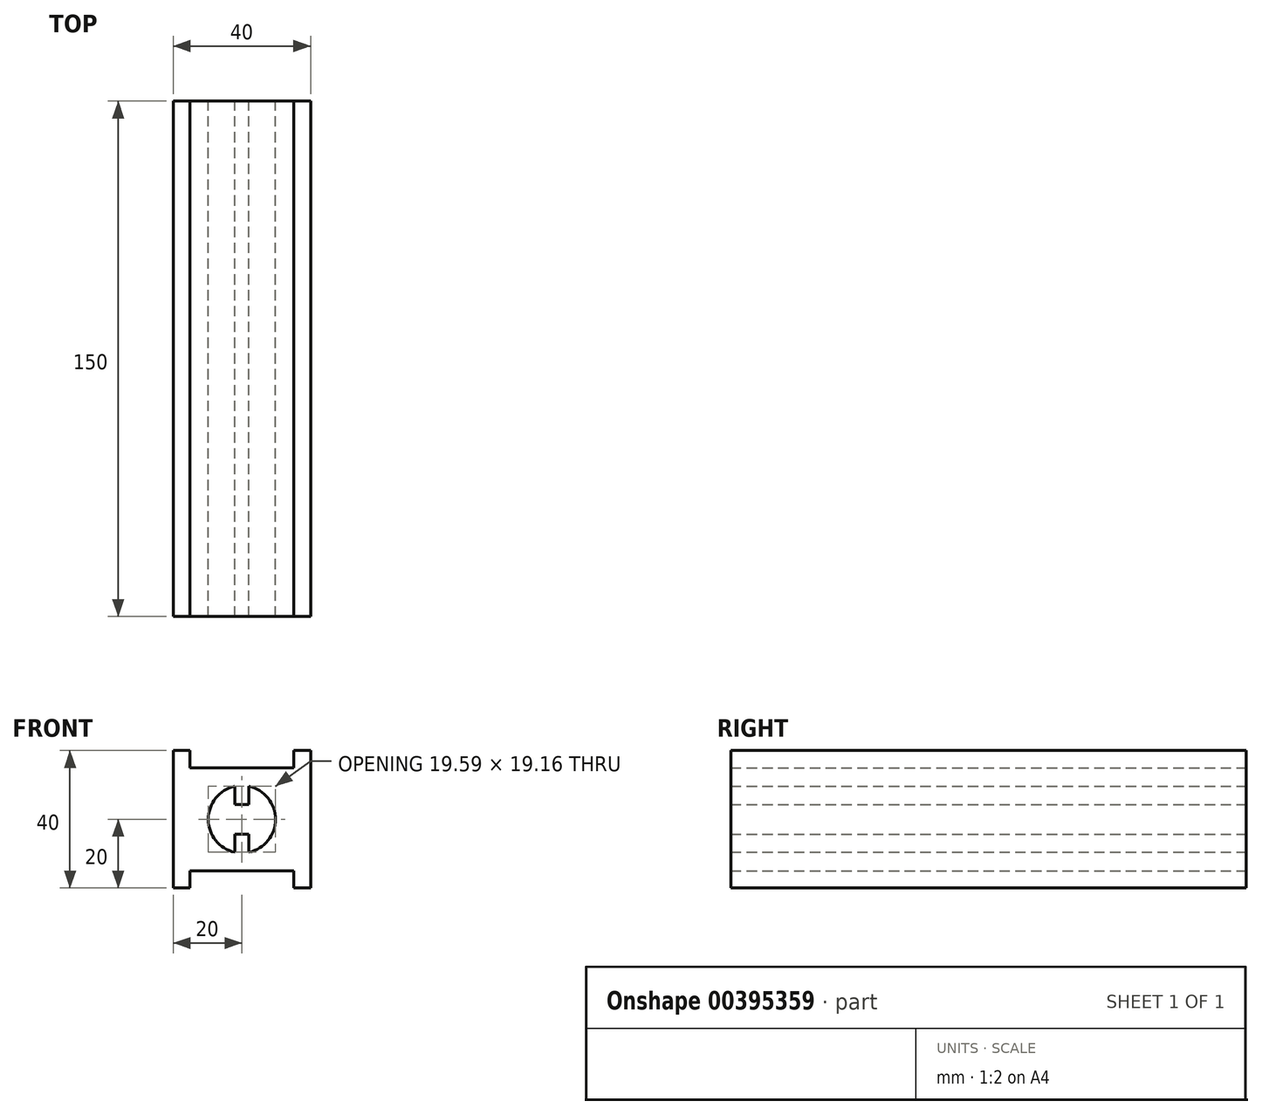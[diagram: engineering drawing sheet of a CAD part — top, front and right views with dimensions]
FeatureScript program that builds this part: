
annotation { "Feature Type Name" : "Feature", "Feature Type Description" : "" }
export const myFeature = defineFeature(function(context is Context, id is Id, definition is map)
    precondition{}
    {
        {
            var Q0;
            Q0=qCreatedBy(makeId("Front.planeOp"),FACE);
            var sketch = newSketch(context, id + "F0", { "sketchPlane" : qUnion([Q0])});
            skLineSegment(sketch, "E0.bottom", {"start": v(20, 20) * mm, "end": v(15.1, 20) * mm});
            skLineSegment(sketch, "E0.top", {"start": v(20, -20) * mm, "end": v(15.1, -20) * mm});
            skLineSegment(sketch, "E0.left", {"start": v(20, 20) * mm, "end": v(20, -20) * mm});
            skLineSegment(sketch, "E0.right", {"start": v(-20, 20) * mm, "end": v(-20, -20) * mm});
            skPoint(sketch, "E0.middle", {"position": v(0, 0) * mm});
            skLineSegment(sketch, "E1.top", {"start": v(-15.1, 15) * mm, "end": v(15.1, 15) * mm});
            skLineSegment(sketch, "E1.left", {"start": v(-15.1, 20) * mm, "end": v(-15.1, 15) * mm});
            skLineSegment(sketch, "E1.right", {"start": v(15.1, 20) * mm, "end": v(15.1, 15) * mm});
            skLineSegment(sketch, "E2.trimOffspring", {"start": v(-15.1, 20) * mm, "end": v(-20, 20) * mm});
            skLineSegment(sketch, "E3.top", {"start": v(-15.1, -15) * mm, "end": v(15.1, -15) * mm});
            skLineSegment(sketch, "E3.left", {"start": v(-15.1, -20) * mm, "end": v(-15.1, -15) * mm});
            skLineSegment(sketch, "E3.right", {"start": v(15.1, -20) * mm, "end": v(15.1, -15) * mm});
            skLineSegment(sketch, "E4.trimOffspring", {"start": v(-15.1, -20) * mm, "end": v(-20, -20) * mm});
            skArc(sketch, "E5", {"start": v(2.05, -9.58) * mm, "mid": v(9.8, 0) * mm, "end": v(2.05, 9.58) * mm});
            skLineSegment(sketch, "E6.top", {"start": v(-2.05, 4.35) * mm, "end": v(2.05, 4.35) * mm});
            skLineSegment(sketch, "E6.left", {"start": v(-2.05, 9.58) * mm, "end": v(-2.05, 4.35) * mm});
            skLineSegment(sketch, "E6.right", {"start": v(2.05, 9.58) * mm, "end": v(2.05, 4.35) * mm});
            skLineSegment(sketch, "E7.top", {"start": v(2.05, -4.35) * mm, "end": v(-2.05, -4.35) * mm});
            skLineSegment(sketch, "E7.left", {"start": v(2.05, -9.58) * mm, "end": v(2.05, -4.35) * mm});
            skLineSegment(sketch, "E7.right", {"start": v(-2.05, -9.58) * mm, "end": v(-2.05, -4.35) * mm});
            skArc(sketch, "E8.trimOffspring", {"start": v(-2.05, 9.58) * mm, "mid": v(-9.8, 0) * mm, "end": v(-2.05, -9.58) * mm});
            skSolve(sketch);
        }
        {
            var Q0;
            Q0 = qSketchRegion(id + "F0", true);
            extrude(context, id + "F1", {"entities" : qUnion([Q0]), "depth" : 150 * mm});
        }
    });
